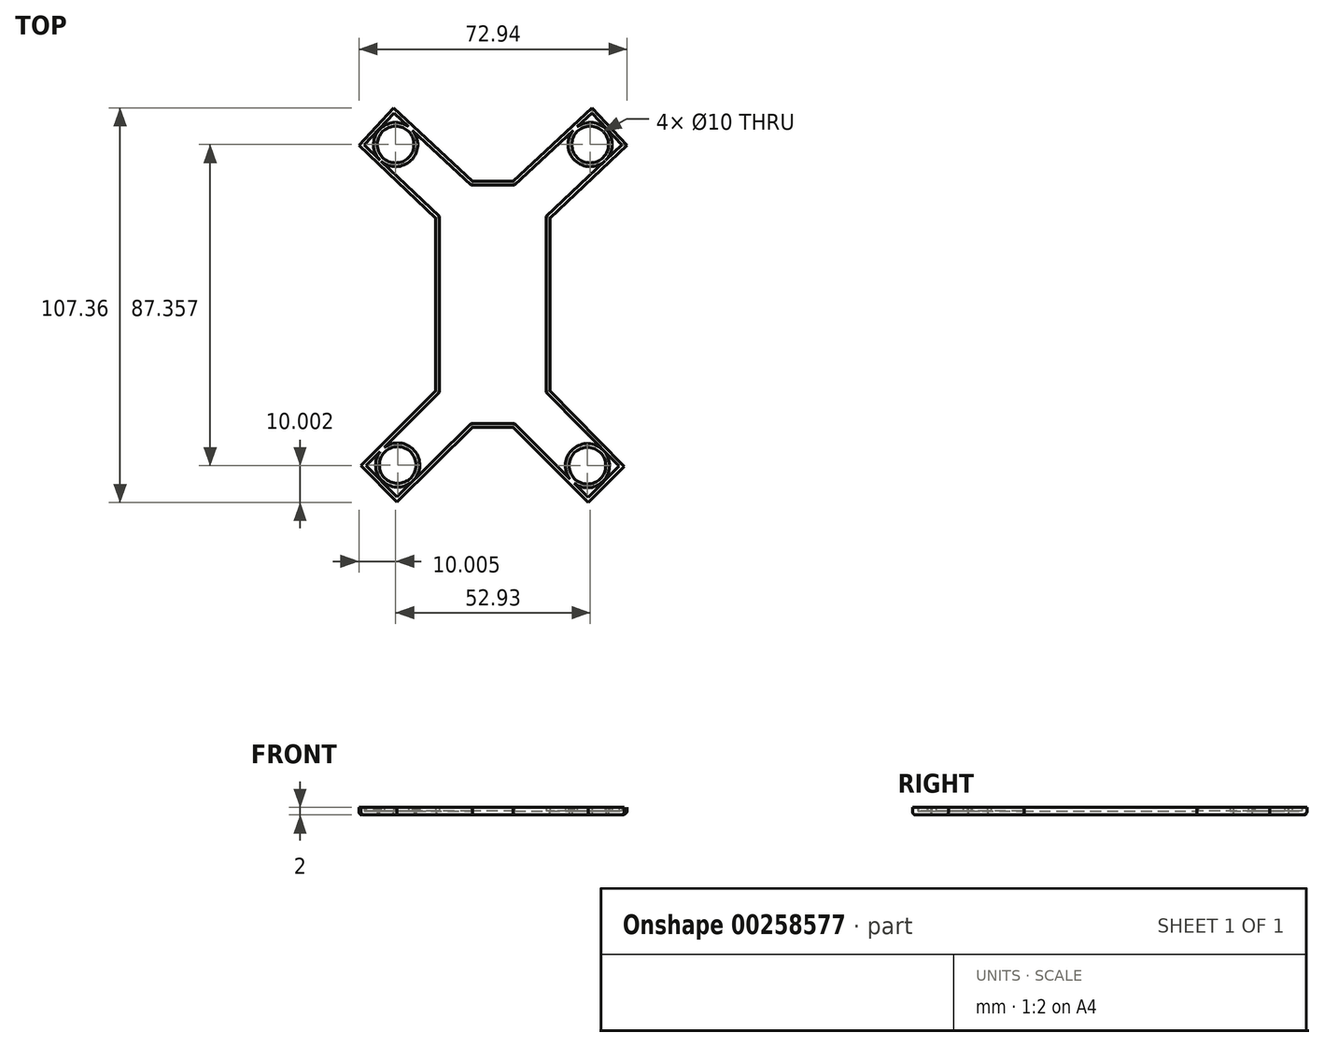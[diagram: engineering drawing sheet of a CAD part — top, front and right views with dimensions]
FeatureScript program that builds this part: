
annotation { "Feature Type Name" : "Feature", "Feature Type Description" : "" }
export const myFeature = defineFeature(function(context is Context, id is Id, definition is map)
    precondition{}
    {
        {
            var Q0;
            Q0=qCreatedBy(makeId("Top.planeOp"),FACE);
            var sketch = newSketch(context, id + "F0", { "sketchPlane" : qUnion([Q0])});
            skLineSegment(sketch, "E0.bottom", {"start": v(5.52, -33.49) * mm, "end": v(-5.52, -33.49) * mm});
            skLineSegment(sketch, "E0.top", {"start": v(5.52, 33.49) * mm, "end": v(-5.52, 33.49) * mm});
            skLineSegment(sketch, "E0.right", {"start": v(-15.52, -23.49) * mm, "end": v(-15.52, 0) * mm});
            skPoint(sketch, "E0.middle", {"position": v(0, 0) * mm});
            skPoint(sketch, "E1.visualSharp", {"position": v(15.52, 33.49) * mm});
            skArc(sketch, "E1.filletArc", {"start": v(15.52, 23.49) * mm, "mid": v(12.59, 30.56) * mm, "end": v(5.52, 33.49) * mm});
            skPoint(sketch, "E2.visualSharp", {"position": v(-15.52, 33.49) * mm});
            skArc(sketch, "E2.filletArc", {"start": v(-5.52, 33.49) * mm, "mid": v(-12.59, 30.56) * mm, "end": v(-15.52, 23.49) * mm});
            skPoint(sketch, "E3.visualSharp", {"position": v(15.52, -33.49) * mm});
            skArc(sketch, "E3.filletArc", {"start": v(5.52, -33.49) * mm, "mid": v(12.59, -30.56) * mm, "end": v(15.52, -23.49) * mm});
            skPoint(sketch, "E4.visualSharp", {"position": v(-15.52, -33.49) * mm});
            skArc(sketch, "E4.filletArc", {"start": v(-15.52, -23.49) * mm, "mid": v(-12.59, -30.56) * mm, "end": v(-5.52, -33.49) * mm});
            skLineSegment(sketch, "E5", {"start": v(5.52, 33.49) * mm, "end": v(27, 53.48) * mm});
            skLineSegment(sketch, "E6", {"start": v(27, 53.48) * mm, "end": v(36.47, 43.3) * mm});
            skLineSegment(sketch, "E7", {"start": v(36.47, 43.3) * mm, "end": v(15.52, 23.49) * mm});
            skPoint(sketch, "E8.MirrorCS.end.orphan", {"position": v(46.1, 33.28) * mm});
            skPoint(sketch, "E8.MirrorCS.start.orphan", {"position": v(24.95, 12.95) * mm});
            skPoint(sketch, "E9.MirrorCS.end.orphan", {"position": v(36.47, 43.3) * mm});
            skLineSegment(sketch, "E10", {"start": v(-5.52, 33.49) * mm, "end": v(-26.99, 53.48) * mm});
            skLineSegment(sketch, "E11", {"start": v(-26.99, 53.48) * mm, "end": v(-36.47, 43.3) * mm});
            skLineSegment(sketch, "E12", {"start": v(-36.47, 43.3) * mm, "end": v(-15.52, 23.49) * mm});
            skPoint(sketch, "E13", {"position": v(-23.77, -55.58) * mm});
            skPoint(sketch, "E14", {"position": v(-36.47, -41.49) * mm});
            skPoint(sketch, "E15", {"position": v(-25.34, -54.43) * mm});
            skPoint(sketch, "E16.end.orphan", {"position": v(-28.2, -50.16) * mm});
            skPoint(sketch, "E16.start.orphan", {"position": v(-36.47, -38.99) * mm});
            skPoint(sketch, "E17.MirrorCS.end.orphan", {"position": v(3.74, 44.17) * mm});
            skPoint(sketch, "E17.MirrorCS.start.orphan", {"position": v(-17.52, 63.66) * mm});
            skPoint(sketch, "E18.MirrorCS.start.orphan", {"position": v(-5.52, 33.49) * mm});
            skPoint(sketch, "E19.MirrorCS.start.orphan", {"position": v(-26.99, 53.48) * mm});
            skPoint(sketch, "E20.MirrorCS.end.orphan", {"position": v(5.95, 13.22) * mm});
            skPoint(sketch, "E20.MirrorCS.start.orphan", {"position": v(-12.32, -9.09) * mm});
            skPoint(sketch, "E21.orphan", {"position": v(-4.73, 22.48) * mm});
            skPoint(sketch, "E22.MirrorCS.end.orphan", {"position": v(-23.15, -0.36) * mm});
            skLineSegment(sketch, "E23", {"start": v(-15.52, 0) * mm, "end": v(15.52, 0) * mm});
            skLineSegment(sketch, "E24", {"start": v(-15.52, 0) * mm, "end": v(-15.52, 23.49) * mm});
            skLineSegment(sketch, "E25", {"start": v(15.52, -23.49) * mm, "end": v(15.52, 0) * mm});
            skLineSegment(sketch, "E26", {"start": v(15.52, 0) * mm, "end": v(15.52, 23.49) * mm});
            skLineSegment(sketch, "E27", {"start": v(5.52, -33.49) * mm, "end": v(25.91, -53.88) * mm});
            skLineSegment(sketch, "E28", {"start": v(25.91, -53.88) * mm, "end": v(35.74, -44.05) * mm});
            skLineSegment(sketch, "E29", {"start": v(35.74, -44.05) * mm, "end": v(15.52, -23.49) * mm});
            skPoint(sketch, "E30.start.orphan", {"position": v(83.73, -44.05) * mm});
            skLineSegment(sketch, "E31", {"start": v(-15.52, -23.49) * mm, "end": v(-35.9, -43.88) * mm});
            skLineSegment(sketch, "E32", {"start": v(-35.9, -43.88) * mm, "end": v(-26.08, -53.71) * mm});
            skLineSegment(sketch, "E33", {"start": v(-26.08, -53.71) * mm, "end": v(-5.52, -33.49) * mm});
            skLineSegment(sketch, "E34", {"start": v(-36.55, 43.3) * mm, "end": v(-14.5, 22.44) * mm});
            skLineSegment(sketch, "E35", {"start": v(-36.55, 43.3) * mm, "end": v(-10.76, 70.97) * mm});
            skPoint(sketch, "E36.start.orphan", {"position": v(25.41, -53.71) * mm});
            skCircle(sketch, "E37", {"center": v(26.47, 43.48) * mm, "radius": 5 * mm});
            skLineSegment(sketch, "E38", {"start": v(-36.47, 43.3) * mm, "end": v(-26.99, 53.48) * mm});
            skPoint(sketch, "E39", {"position": v(-31.73, 48.4) * mm});
            skLineSegment(sketch, "E40", {"start": v(-36.47, 43.3) * mm, "end": v(-31.2, 38.4) * mm});
            skLineSegment(sketch, "E41", {"start": v(-31.2, 38.4) * mm, "end": v(-26.46, 43.48) * mm});
            skCircle(sketch, "E42", {"center": v(-26.46, 43.48) * mm, "radius": 5 * mm});
            skPoint(sketch, "E43", {"position": v(-31, -48.8) * mm});
            skLineSegment(sketch, "E44", {"start": v(-26.08, -53.71) * mm, "end": v(-20.99, -48.62) * mm});
            skLineSegment(sketch, "E45", {"start": v(-20.99, -48.62) * mm, "end": v(-25.9, -43.71) * mm});
            skCircle(sketch, "E46", {"center": v(-25.9, -43.71) * mm, "radius": 5 * mm});
            skLineSegment(sketch, "E47", {"start": v(35.74, -44.05) * mm, "end": v(30.65, -38.96) * mm});
            skLineSegment(sketch, "E48", {"start": v(30.65, -38.96) * mm, "end": v(25.73, -43.88) * mm});
            skCircle(sketch, "E49", {"center": v(25.73, -43.88) * mm, "radius": 5 * mm});
            skSolve(sketch);
        }
        {
            var Q0;
            Q0=qCreatedBy(makeId("Top.planeOp"),FACE);
            var sketch = newSketch(context, id + "F1", { "sketchPlane" : qUnion([Q0])});
            skLineSegment(sketch, "E50", {"start": v(-15.52, -23.49) * mm, "end": v(-35.9, -43.88) * mm});
            skLineSegment(sketch, "E51", {"start": v(-35.9, -43.88) * mm, "end": v(-26.08, -53.71) * mm});
            skLineSegment(sketch, "E52", {"start": v(-26.08, -53.71) * mm, "end": v(-5.52, -33.49) * mm});
            skLineSegment(sketch, "E53", {"start": v(-36.47, 43.3) * mm, "end": v(-15.52, 23.49) * mm});
            skLineSegment(sketch, "E54", {"start": v(-36.47, 43.3) * mm, "end": v(-26.99, 53.48) * mm});
            skPoint(sketch, "E55.start.orphan", {"position": v(25.41, -53.71) * mm});
            skSolve(sketch);
        }
        {
            var Q0;
            Q0=qCreatedBy(makeId("Top.planeOp"),FACE);
            var sketch = newSketch(context, id + "F2", { "sketchPlane" : qUnion([Q0])});
            skLineSegment(sketch, "E56", {"start": v(5.52, -33.49) * mm, "end": v(25.91, -53.88) * mm});
            skLineSegment(sketch, "E57", {"start": v(25.91, -53.88) * mm, "end": v(35.74, -44.05) * mm});
            skLineSegment(sketch, "E58", {"start": v(35.74, -44.05) * mm, "end": v(15.52, -23.49) * mm});
            skPoint(sketch, "E59.start.orphan", {"position": v(83.73, -44.05) * mm});
            skSolve(sketch);
        }
        {
            var Q0;
            Q0=qCreatedBy(makeId("Top.planeOp"),FACE);
            var sketch = newSketch(context, id + "F3", { "sketchPlane" : qUnion([Q0])});
            skLineSegment(sketch, "E60", {"start": v(27, 53.48) * mm, "end": v(36.47, 43.3) * mm});
            skCircle(sketch, "E61", {"center": v(26.47, 43.48) * mm, "radius": 5 * mm});
            skLineSegment(sketch, "E62", {"start": v(-36.47, 43.3) * mm, "end": v(-26.99, 53.48) * mm});
            skPoint(sketch, "E63", {"position": v(-31.73, 48.4) * mm});
            skLineSegment(sketch, "E64", {"start": v(-36.47, 43.3) * mm, "end": v(-31.2, 38.4) * mm});
            skLineSegment(sketch, "E65", {"start": v(-31.2, 38.4) * mm, "end": v(-26.46, 43.48) * mm});
            skCircle(sketch, "E66", {"center": v(-26.46, 43.48) * mm, "radius": 5 * mm});
            skLineSegment(sketch, "E67", {"start": v(-35.9, -43.88) * mm, "end": v(-26.08, -53.71) * mm});
            skPoint(sketch, "E68", {"position": v(-31, -48.8) * mm});
            skLineSegment(sketch, "E69", {"start": v(-26.08, -53.71) * mm, "end": v(-20.99, -48.62) * mm});
            skLineSegment(sketch, "E70", {"start": v(-20.99, -48.62) * mm, "end": v(-25.9, -43.71) * mm});
            skCircle(sketch, "E71", {"center": v(-25.9, -43.71) * mm, "radius": 5 * mm});
            skLineSegment(sketch, "E72", {"start": v(25.91, -53.88) * mm, "end": v(35.74, -44.05) * mm});
            skLineSegment(sketch, "E73", {"start": v(35.74, -44.05) * mm, "end": v(30.65, -38.96) * mm});
            skLineSegment(sketch, "E74", {"start": v(30.65, -38.96) * mm, "end": v(25.73, -43.88) * mm});
            skCircle(sketch, "E75", {"center": v(25.73, -43.88) * mm, "radius": 5 * mm});
            skSolve(sketch);
        }
        {
            var Q0;
            Q0=makeQuery(id+"F0.imprint","IMPRINT",FACE,{"disambiguationData":[TD([[makeQuery(id+"F0.imprint","IMPRINT",EDGE,{"derivedFrom":sQuery(id+"F0.wireOp",EDGE,"E0.top")}),1.0]])]});
            var Q1;
            Q1=makeQuery(id+"F0.imprint","IMPRINT",FACE,{"disambiguationData":[TD([[makeQuery(id+"F0.imprint","IMPRINT",EDGE,{"derivedFrom":sQuery(id+"F0.wireOp",EDGE,"E0.bottom")}),-1.0]])]});
            var Q2;
            Q2=makeQuery(id+"F0.imprint","IMPRINT",FACE,{"disambiguationData":[TD([[makeQuery(id+"F0.imprint","IMPRINT",EDGE,{"derivedFrom":sQuery(id+"F0.wireOp",EDGE,"E2.filletArc")}),-1.0]])]});
            var Q3;
            Q3=makeQuery(id+"F0.imprint","IMPRINT",FACE,{"disambiguationData":[TD([[makeQuery(id+"F0.imprint","IMPRINT",EDGE,{"derivedFrom":sQuery(id+"F0.wireOp",EDGE,"E1.filletArc")}),-1.0]])]});
            var Q4;
            Q4=makeQuery(id+"F0.imprint","IMPRINT",FACE,{"disambiguationData":[TD([[makeQuery(id+"F0.imprint","IMPRINT",EDGE,{"derivedFrom":sQuery(id+"F0.wireOp",EDGE,"E4.filletArc")}),-1.0]])]});
            var Q5;
            Q5=makeQuery(id+"F0.imprint","IMPRINT",FACE,{"disambiguationData":[TD([[makeQuery(id+"F0.imprint","IMPRINT",EDGE,{"derivedFrom":sQuery(id+"F0.wireOp",EDGE,"E3.filletArc")}),-1.0]])]});
            extrude(context, id + "F4", {"entities" : qUnion([Q0, Q1, Q2, Q3, Q4, Q5]), "depth" : 2 * mm});
        }
        {
            var Q0;
            Q0 = qSketchRegion(id + "F3", true);
            extrude(context, id + "F5", {"entities" : qUnion([Q0]), "operationType" : NewBodyOperationType.REMOVE, "oppositeDirection" : true, "depth" : 25 * mm});
        }
        {
            var Q0;
            Q0=makeQuery(id+"F4.opExtrude","CAP_FACE",FACE,{"disambiguationData":[OSD([sQuery(id+"F0.wireOp",EDGE,"E0.bottom"),sQuery(id+"F0.wireOp",EDGE,"E0.top"),sQuery(id+"F0.wireOp",EDGE,"E0.right"),sQuery(id+"F0.wireOp",EDGE,"E5"),sQuery(id+"F0.wireOp",EDGE,"E7"),sQuery(id+"F0.wireOp",EDGE,"E10"),sQuery(id+"F0.wireOp",EDGE,"E12"),sQuery(id+"F0.wireOp",EDGE,"E24"),sQuery(id+"F0.wireOp",EDGE,"E25"),sQuery(id+"F0.wireOp",EDGE,"E26"),sQuery(id+"F0.wireOp",EDGE,"E27"),sQuery(id+"F0.wireOp",EDGE,"E29"),sQuery(id+"F0.wireOp",EDGE,"E31"),sQuery(id+"F0.wireOp",EDGE,"E33"),sQuery(id+"F0.wireOp",EDGE,"E6"),sQuery(id+"F0.wireOp",EDGE,"E37"),sQuery(id+"F0.wireOp",EDGE,"E38"),sQuery(id+"F0.wireOp",EDGE,"E42"),sQuery(id+"F0.wireOp",EDGE,"E32"),sQuery(id+"F0.wireOp",EDGE,"E46"),sQuery(id+"F0.wireOp",EDGE,"E28"),sQuery(id+"F0.wireOp",EDGE,"E49")])],"isStart":false});
            shell(context, id + "F6", {"entities" : qUnion([Q0]), "thickness" : 1 * mm});
        }
        {
            var Q0;
            Q0=makeQuery(id+"F4.opExtrude","CAP_EDGE",EDGE,{"disambiguationData":[OSD([sQuery(id+"F0.wireOp",EDGE,"E0.top")])],"isStart":true});
            var Q1;
            Q1=makeQuery(id+"F4.opExtrude","CAP_EDGE",EDGE,{"disambiguationData":[OSD([sQuery(id+"F0.wireOp",EDGE,"E5")])],"isStart":true});
            var Q2;
            Q2=makeQuery(id+"F4.opExtrude","CAP_EDGE",EDGE,{"disambiguationData":[OSD([sQuery(id+"F0.wireOp",EDGE,"E10")])],"isStart":true});
            var Q3;
            Q3=makeQuery(id+"F4.opExtrude","CAP_EDGE",EDGE,{"disambiguationData":[OSD([sQuery(id+"F0.wireOp",EDGE,"E12")])],"isStart":true});
            var Q4;
            Q4=makeQuery(id+"F4.opExtrude","CAP_EDGE",EDGE,{"disambiguationData":[OSD([sQuery(id+"F0.wireOp",EDGE,"E25"),sQuery(id+"F0.wireOp",EDGE,"E26")])],"isStart":true});
            var Q5;
            Q5=makeQuery(id+"F4.opExtrude","CAP_EDGE",EDGE,{"disambiguationData":[OSD([sQuery(id+"F0.wireOp",EDGE,"E7")])],"isStart":true});
            var Q6;
            Q6=makeQuery(id+"F4.opExtrude","CAP_EDGE",EDGE,{"disambiguationData":[OSD([sQuery(id+"F0.wireOp",EDGE,"E0.right"),sQuery(id+"F0.wireOp",EDGE,"E24")])],"isStart":true});
            var Q7;
            Q7=makeQuery(id+"F4.opExtrude","CAP_EDGE",EDGE,{"disambiguationData":[OSD([sQuery(id+"F0.wireOp",EDGE,"E31")])],"isStart":true});
            var Q8;
            Q8=makeQuery(id+"F4.opExtrude","CAP_EDGE",EDGE,{"disambiguationData":[OSD([sQuery(id+"F0.wireOp",EDGE,"E32")])],"isStart":true});
            var Q9;
            Q9=makeQuery(id+"F4.opExtrude","CAP_EDGE",EDGE,{"disambiguationData":[OSD([sQuery(id+"F0.wireOp",EDGE,"E33")])],"isStart":true});
            var Q10;
            Q10=makeQuery(id+"F4.opExtrude","CAP_EDGE",EDGE,{"disambiguationData":[OSD([sQuery(id+"F0.wireOp",EDGE,"E0.bottom")])],"isStart":true});
            var Q11;
            Q11=makeQuery(id+"F4.opExtrude","CAP_EDGE",EDGE,{"disambiguationData":[OSD([sQuery(id+"F0.wireOp",EDGE,"E27")])],"isStart":true});
            var Q12;
            Q12=makeQuery(id+"F4.opExtrude","CAP_EDGE",EDGE,{"disambiguationData":[OSD([sQuery(id+"F0.wireOp",EDGE,"E29")])],"isStart":true});
            var Q13;
            Q13=makeQuery(id+"F4.opExtrude","CAP_EDGE",EDGE,{"disambiguationData":[OSD([sQuery(id+"F0.wireOp",EDGE,"E28")])],"isStart":true});
            var Q14;
            Q14=makeQuery(id+"F4.opExtrude","CAP_EDGE",EDGE,{"disambiguationData":[OSD([sQuery(id+"F0.wireOp",EDGE,"E6")])],"isStart":true});
            var Q15;
            Q15=makeQuery(id+"F4.opExtrude","CAP_EDGE",EDGE,{"disambiguationData":[OSD([sQuery(id+"F0.wireOp",EDGE,"E38")])],"isStart":true});
            fillet(context, id + "F7", {"entities" : qUnion([Q0, Q1, Q2, Q3, Q4, Q5, Q6, Q7, Q8, Q9, Q10, Q11, Q12, Q13, Q14, Q15]), "radius" : 1 * mm, "tangentPropagation" : true, "allowEdgeOverflow" : false});
        }
    });
